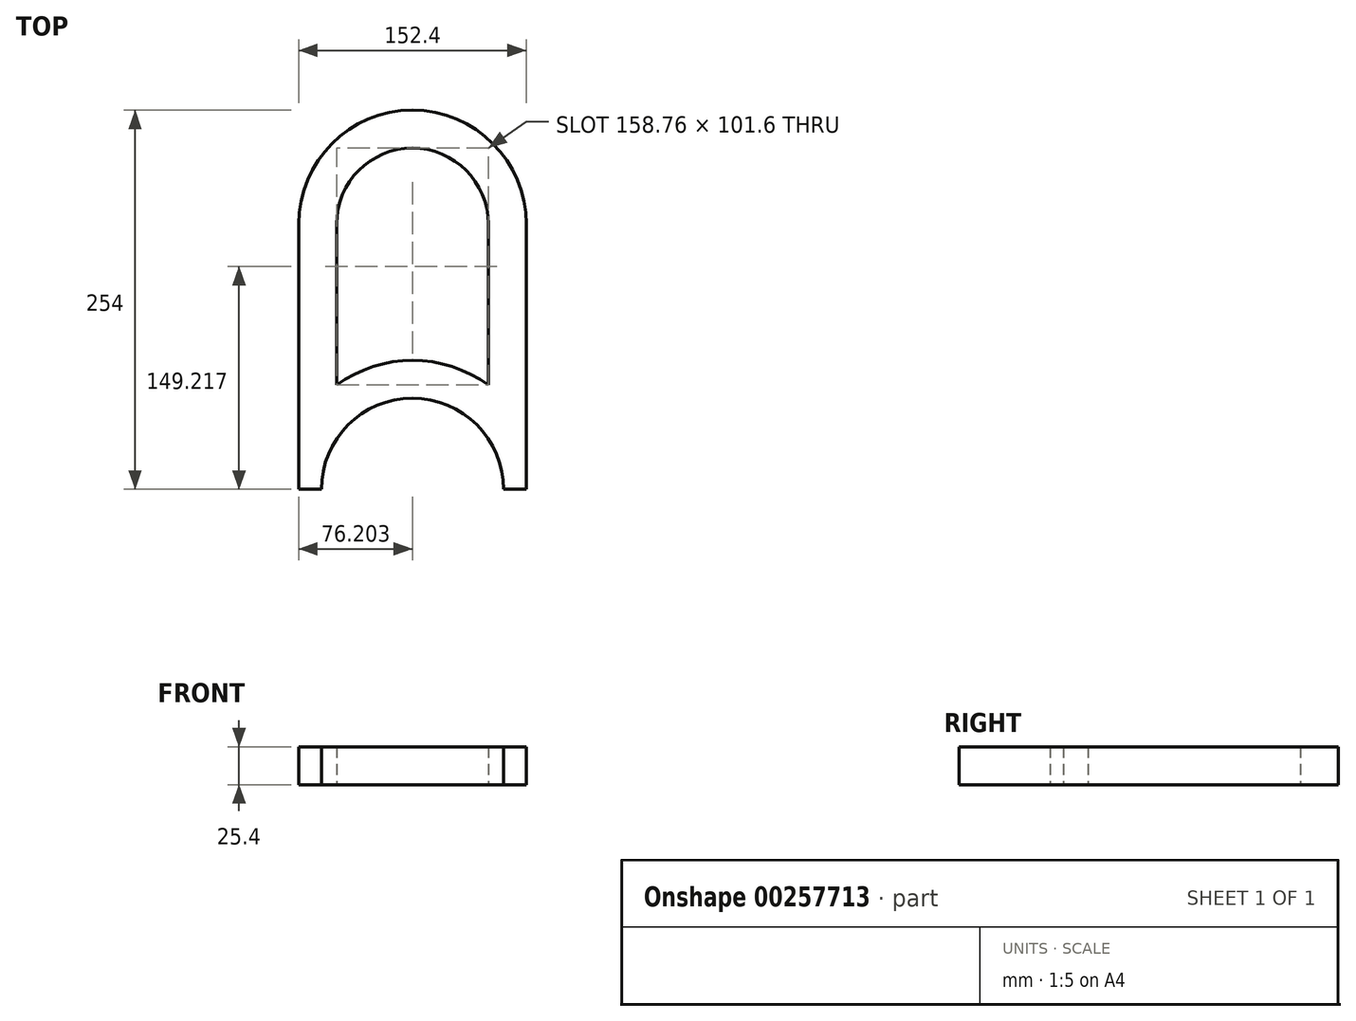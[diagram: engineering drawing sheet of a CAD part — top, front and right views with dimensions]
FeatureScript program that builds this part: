
annotation { "Feature Type Name" : "Feature", "Feature Type Description" : "" }
export const myFeature = defineFeature(function(context is Context, id is Id, definition is map)
    precondition{}
    {
        {
            var Q0;
            Q0=qCreatedBy(makeId("Top.planeOp"),FACE);
            var sketch = newSketch(context, id + "F0", { "sketchPlane" : qUnion([Q0])});
            skLineSegment(sketch, "E0", {"start": v(198.33, -48.37) * mm, "end": v(198.33, 129.43) * mm});
            skLineSegment(sketch, "E1", {"start": v(274.53, 205.63) * mm, "end": v(350.73, 205.63) * mm});
            skLineSegment(sketch, "E2", {"start": v(350.73, 129.43) * mm, "end": v(350.73, -48.37) * mm});
            skLineSegment(sketch, "E3", {"start": v(350.73, -48.37) * mm, "end": v(335.5, -48.37) * mm});
            skLineSegment(sketch, "E4", {"start": v(274.53, 205.63) * mm, "end": v(274.53, 205.63) * mm});
            skPoint(sketch, "E5.visualSharp", {"position": v(350.73, 205.63) * mm});
            skArc(sketch, "E5.filletArc", {"start": v(350.73, 129.43) * mm, "mid": v(328.41, 183.3) * mm, "end": v(274.53, 205.63) * mm});
            skPoint(sketch, "E6.visualSharp", {"position": v(198.33, 205.63) * mm});
            skArc(sketch, "E6.filletArc", {"start": v(274.53, 205.63) * mm, "mid": v(220.65, 183.3) * mm, "end": v(198.33, 129.43) * mm});
            skLineSegment(sketch, "E7", {"start": v(198.33, -48.37) * mm, "end": v(213.57, -48.37) * mm});
            skPoint(sketch, "E8", {"position": v(274.53, -48.37) * mm});
            skArc(sketch, "E9", {"start": v(335.5, -48.37) * mm, "mid": v(274.53, 12.59) * mm, "end": v(213.57, -48.37) * mm});
            skLineSegment(sketch, "E10.trimOffspring", {"start": v(213.57, -48.37) * mm, "end": v(198.33, -48.37) * mm});
            skLineSegment(sketch, "E11", {"start": v(274.53, 205.63) * mm, "end": v(274.53, 180.23) * mm});
            skArc(sketch, "E12", {"start": v(325.33, 129.43) * mm, "mid": v(274.53, 180.23) * mm, "end": v(223.73, 129.43) * mm});
            skArc(sketch, "E13", {"start": v(325.33, 21.47) * mm, "mid": v(274.53, 37.99) * mm, "end": v(223.73, 21.47) * mm});
            skLineSegment(sketch, "E14", {"start": v(325.33, 129.43) * mm, "end": v(325.33, 21.47) * mm});
            skLineSegment(sketch, "E15", {"start": v(223.73, 129.43) * mm, "end": v(223.73, 21.47) * mm});
            skSolve(sketch);
        }
        {
            var Q0;
            Q0 = qSketchRegion(id + "F0", true);
            extrude(context, id + "F1", {"entities" : qUnion([Q0]), "depth" : 25.4 * mm});
        }
    });
